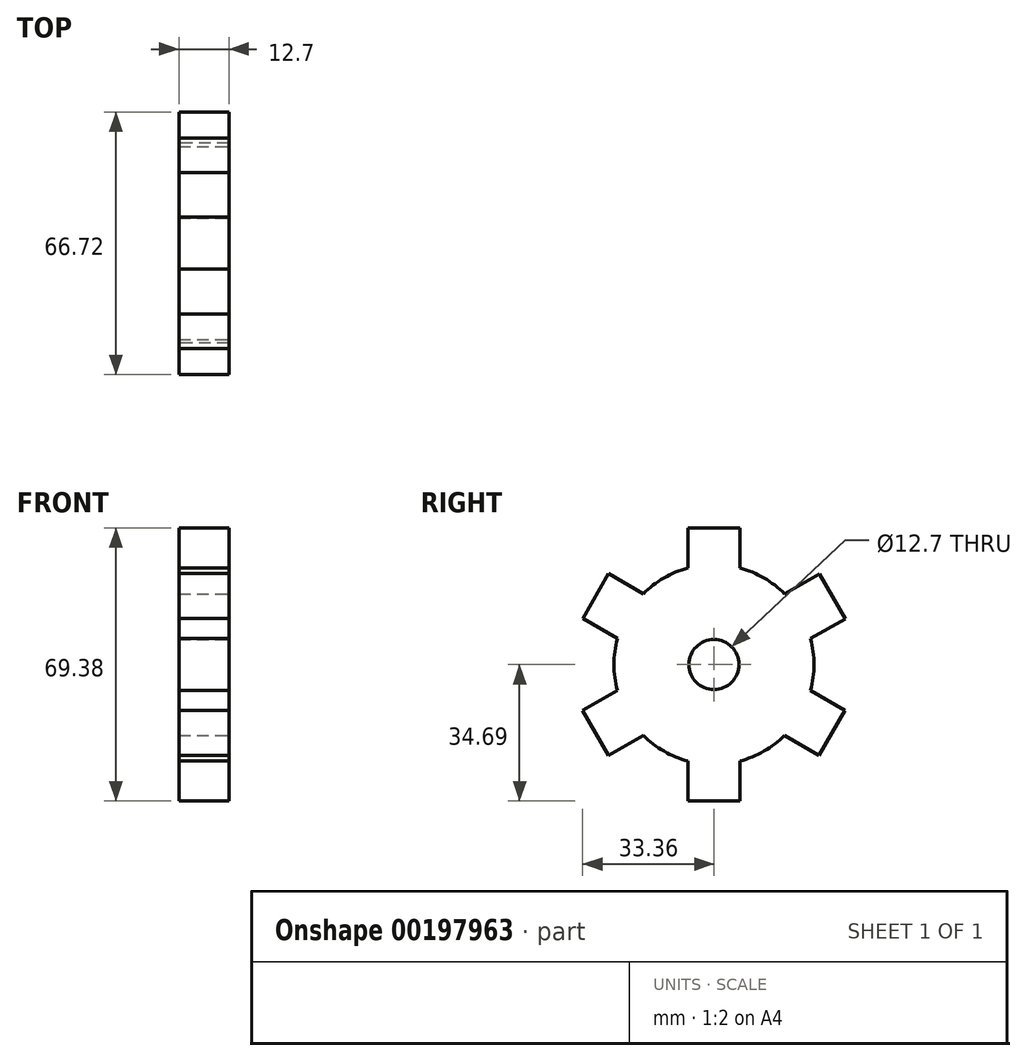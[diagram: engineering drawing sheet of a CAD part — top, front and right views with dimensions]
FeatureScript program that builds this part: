
annotation { "Feature Type Name" : "Feature", "Feature Type Description" : "" }
export const myFeature = defineFeature(function(context is Context, id is Id, definition is map)
    precondition{}
    {
        {
            var Q0;
            Q0=qCreatedBy(makeId("Right.planeOp"),FACE);
            var sketch = newSketch(context, id + "F0", { "sketchPlane" : qUnion([Q0])});
            skCircle(sketch, "E0", {"center": v(0, 0) * mm, "radius": 25.4 * mm});
            skSolve(sketch);
        }
        {
            var Q0;
            Q0 = qSketchRegion(id + "F0", true);
            extrude(context, id + "F1", {"entities" : qUnion([Q0]), "endBound" : BoundingType.SYMMETRIC, "depth" : 12.7 * mm});
        }
        {
            var Q0;
            Q0=makeQuery(id+"F1.opExtrude","CAP_FACE",FACE,{"disambiguationData":[OSD([sQuery(id+"F0.wireOp",EDGE,"E0")])],"isStart":false});
            var sketch = newSketch(context, id + "F2", { "sketchPlane" : qUnion([Q0])});
            skLineSegment(sketch, "E1", {"start": v(0, 0) * mm, "end": v(0, 25.4) * mm});
            skLineSegment(sketch, "E2", {"start": v(0, 0) * mm, "end": v(6.57, 24.53) * mm});
            skLineSegment(sketch, "E3", {"start": v(0, 0) * mm, "end": v(-6.57, 24.53) * mm});
            skLineSegment(sketch, "E4", {"start": v(-6.57, 24.53) * mm, "end": v(6.57, 24.53) * mm});
            skLineSegment(sketch, "E5.0", {"start": v(-6.57, 34.7) * mm, "end": v(6.63, 34.7) * mm});
            skLineSegment(sketch, "E6", {"start": v(-6.57, 34.7) * mm, "end": v(-6.57, 24.53) * mm});
            skLineSegment(sketch, "E7", {"start": v(6.63, 34.7) * mm, "end": v(6.57, 24.53) * mm});
            skSolve(sketch);
        }
        {
            var Q0;
            Q0 = qSketchRegion(id + "F2", true);
            extrude(context, id + "F3", {"entities" : qUnion([Q0]), "operationType" : NewBodyOperationType.ADD, "oppositeDirection" : true, "depth" : 12.7 * mm});
        }
        {
            var Q0;
            Q0=qCreatedBy(makeId("Top.planeOp"),FACE);
            var sketch = newSketch(context, id + "F4", { "sketchPlane" : qUnion([Q0])});
            skLineSegment(sketch, "E8", {"start": v(0, 0) * mm, "end": v(-63.16, 0) * mm});
            skSolve(sketch);
        }
        {
            var Q0;
            Q0=makeQuery(id+"F1.opExtrude","SWEPT_BODY",BODY,{"disambiguationData":[OSD([sQuery(id+"F0.wireOp",EDGE,"E0")])]});
            var Q1;
            Q1=sQuery(id+"F4.wireOp",EDGE,"E8");
            circularPattern(context, id + "F5", {"operationType" : NewBodyOperationType.ADD, "entities" : qUnion([Q0]), "axis" : qUnion([Q1]), "angle" : 360 * degree, "instanceCount" : 6, "equalSpace" : true});
        }
        {
            var Q0;
            {var subQ0=makeQuery(id+"F3.boolean.opBoolean","MERGE",FACE,{"derivedFrom":[makeQuery(id+"F1.opExtrude","CAP_FACE",FACE,{"disambiguationData":[OSD([sQuery(id+"F0.wireOp",EDGE,"E0")])],"isStart":false}),makeQuery(id+"F3.opExtrude","CAP_FACE",FACE,{"disambiguationData":[OSD([sQuery(id+"F2.wireOp",EDGE,"E2"),sQuery(id+"F2.wireOp",EDGE,"E3"),sQuery(id+"F2.wireOp",EDGE,"E5.0"),sQuery(id+"F2.wireOp",EDGE,"E6"),sQuery(id+"F2.wireOp",EDGE,"E7")])],"isStart":true})]});Q0=makeQuery(id+"F5.boolean.opBoolean","MERGE",FACE,{"derivedFrom":[subQ0,makeQuery(id+"F5.opPattern","COPY",FACE,{"derivedFrom":subQ0,"instanceName":"1"}),makeQuery(id+"F5.opPattern","COPY",FACE,{"derivedFrom":subQ0,"instanceName":"2"}),makeQuery(id+"F5.opPattern","COPY",FACE,{"derivedFrom":subQ0,"instanceName":"3"}),makeQuery(id+"F5.opPattern","COPY",FACE,{"derivedFrom":subQ0,"instanceName":"4"}),makeQuery(id+"F5.opPattern","COPY",FACE,{"derivedFrom":subQ0,"instanceName":"5"})]});}
            var sketch = newSketch(context, id + "F6", { "sketchPlane" : qUnion([Q0])});
            skCircle(sketch, "E9", {"center": v(0, 0) * mm, "radius": 6.35 * mm});
            skSolve(sketch);
        }
        {
            var Q0;
            Q0 = qSketchRegion(id + "F6", true);
            extrude(context, id + "F7", {"entities" : qUnion([Q0]), "operationType" : NewBodyOperationType.REMOVE, "oppositeDirection" : true, "depth" : 25.4 * mm});
        }
    });
